# Revit family: Ceiling-Fan_Residential
name_source: partatom
category: Mechanical Equipment
units: mm (PartAtom-declared; Revit-internal decimal feet)

## family parameters
Always vertical = Yes
Classification Number = 23.75.35.17
Cut with Voids When Loaded = No
Host = Ceiling
Maintain Annotation Orientation = No
Part Type = Normal
Room Calculation Point = No
Round Connector Dimension = Use Diameter
Shared = No

## types (4) — shared parameters
Air Flow Efficiency = 155, 110, 75, CFM / Watt
Assembly Code = D3040
Blade Pitch = 20.00°
Body Color = Plastic, White
Construction Details = http://www.arcat.com
Default Elevation = 0' - 0"
Description = Residential Ceiling Fan
ENERGYSTAR = http://www.energystar.gov
ENERGYSTAR Rated = No
Fan Blade Finish = Wood - Cherry
Fan Speed = 1250, 2500, 5000 CFM
Green Building-LEED = http://www.arcat.com
Hardware Accent Finish = Metal - Brass, Polished
Keynote = 15830
Manufacturer = Generic
Manufacturer Fax = (203) 929-2444
Manufacturer Website = http://www.arcat.com
Model = Generic
Operating Range = 20' - 0"
Power Consumption_Fan = 66
Product Data = http://www.arcat.com
Product Properties = http://www.arcat.com
Sound Pressure Level (dB) = 10
Specification = http://www.arcat.com
URL = http://www.arcat.com
zero-valued in all types: Expected Lifespan (Years), Maintenance Schedule (Months), Warranty Duration (Years)

## per-type parameters (varying)
| type | Blade Length | Pull Cord Finish | Span |
| 52" | 1' - 6 5/16" | ARCAT - Plastic, ABS - White | 4' - 4" |
| 48" | 1' - 4 5/16" | Metal - Brass, Polished | 4' - 0" |
| 60" | 1' - 10 5/16" | Metal - Brass, Polished | 5' - 0" |
| 36" | 0' - 10 5/16" | Metal - Brass, Polished | 3' - 0" |

## geometry (parser evidence)
native form markers: Sweep x7
no freeform markers — native parametric forms only
